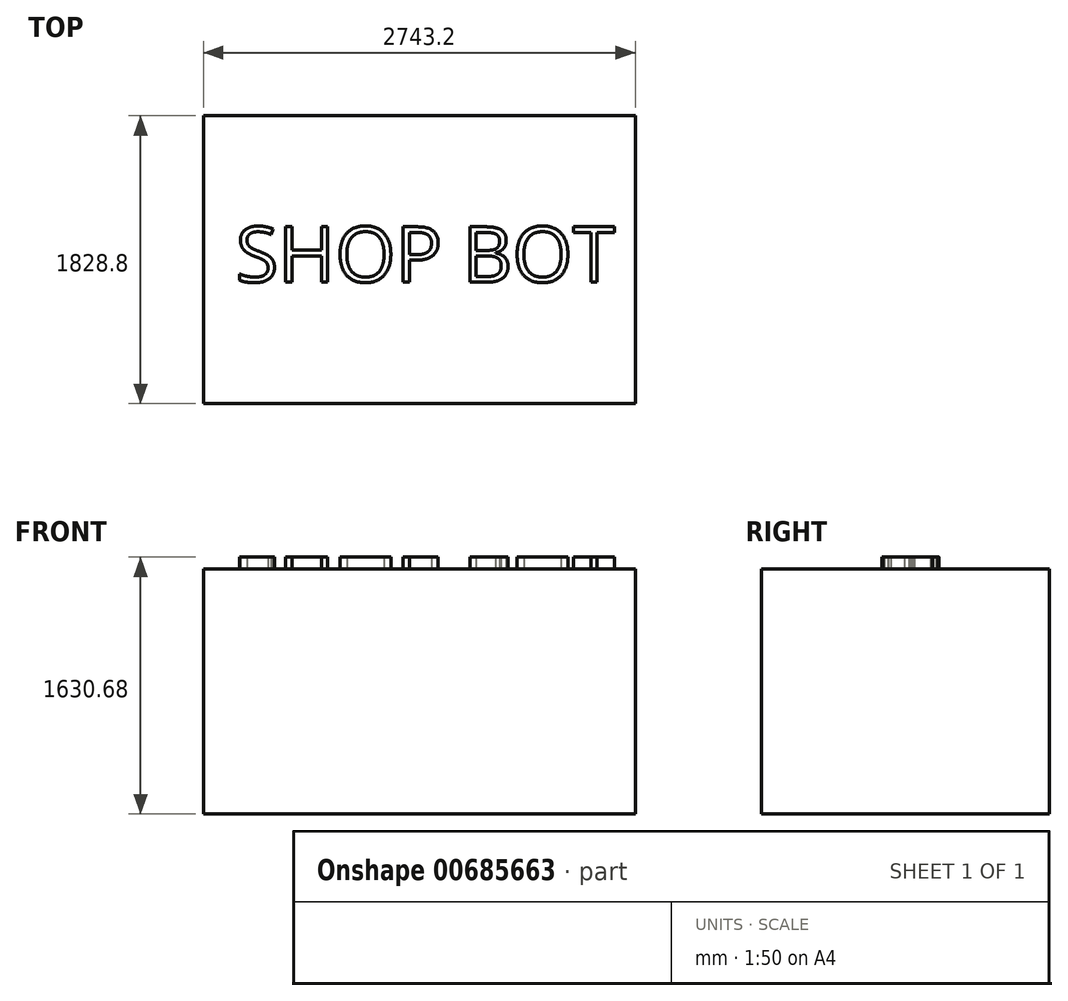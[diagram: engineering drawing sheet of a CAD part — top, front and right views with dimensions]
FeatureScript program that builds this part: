
annotation { "Feature Type Name" : "Feature", "Feature Type Description" : "" }
export const myFeature = defineFeature(function(context is Context, id is Id, definition is map)
    precondition{}
    {
        {
            var Q0;
            Q0=qCreatedBy(makeId("Top.planeOp"),FACE);
            var sketch = newSketch(context, id + "F0", { "sketchPlane" : qUnion([Q0])});
            skLineSegment(sketch, "E0.bottom", {"start": v(1371.6, 914.4) * mm, "end": v(-1371.6, 914.4) * mm});
            skLineSegment(sketch, "E0.top", {"start": v(1371.6, -914.4) * mm, "end": v(-1371.6, -914.4) * mm});
            skLineSegment(sketch, "E0.left", {"start": v(1371.6, 914.4) * mm, "end": v(1371.6, -914.4) * mm});
            skLineSegment(sketch, "E0.right", {"start": v(-1371.6, 914.4) * mm, "end": v(-1371.6, -914.4) * mm});
            skPoint(sketch, "E0.middle", {"position": v(0, 0) * mm});
            skSolve(sketch);
        }
        {
            var Q0;
            Q0 = qSketchRegion(id + "F0", true);
            extrude(context, id + "F1", {"entities" : qUnion([Q0]), "depth" : 1554.48 * mm, "offsetDistance" : 30.48 * mm});
        }
        {
            var Q0;
            Q0=makeQuery(id+"F1.opExtrude","CAP_FACE",FACE,{"disambiguationData":[OSD([sQuery(id+"F0.wireOp",EDGE,"E0.bottom"),sQuery(id+"F0.wireOp",EDGE,"E0.top"),sQuery(id+"F0.wireOp",EDGE,"E0.left"),sQuery(id+"F0.wireOp",EDGE,"E0.right")])],"isStart":false});
            var sketch = newSketch(context, id + "F2", { "sketchPlane" : qUnion([Q0])});
            skText(sketch, "E1", { "text": "SHOP BOT", "fontName": "OpenSans-Regular.ttf"});
            const initialGuessF2  = {"E1": [-1.16617, -0.14206, 1, 0, 0.35376]};
            skSetInitialGuess(sketch, initialGuessF2);
            skSolve(sketch);
        }
        {
            var Q0;
            Q0 = qSketchRegion(id + "F2", true);
            extrude(context, id + "F3", {"entities" : qUnion([Q0]), "operationType" : NewBodyOperationType.ADD, "depth" : 76.2 * mm, "offsetDistance" : 30.48 * mm});
        }
    });
